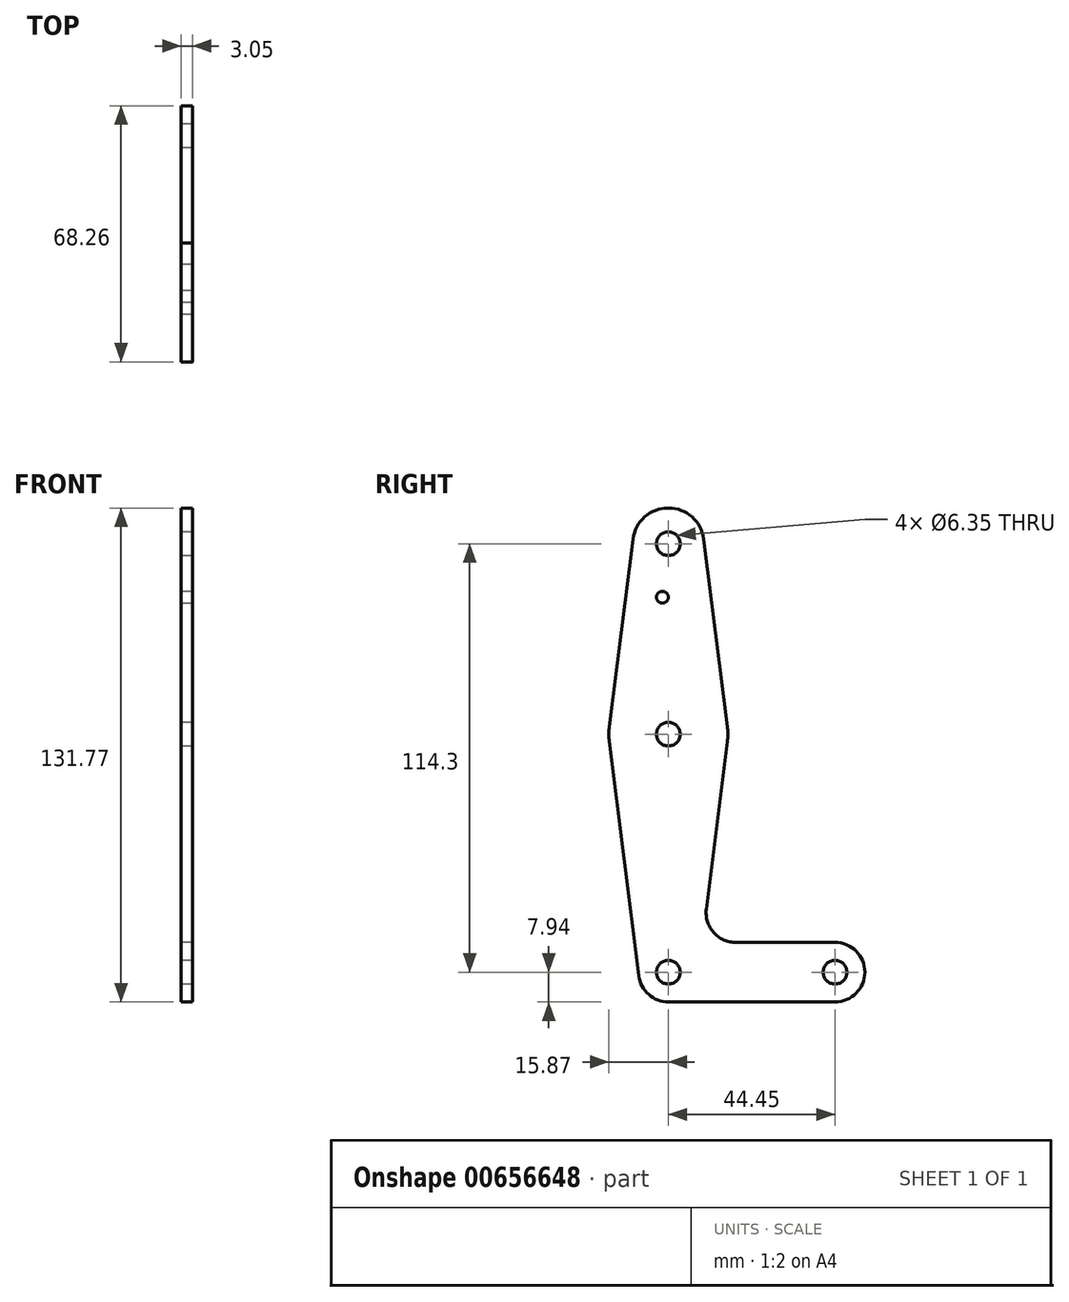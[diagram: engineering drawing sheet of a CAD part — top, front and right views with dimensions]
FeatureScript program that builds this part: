
annotation { "Feature Type Name" : "Feature", "Feature Type Description" : "" }
export const myFeature = defineFeature(function(context is Context, id is Id, definition is map)
    precondition{}
    {
        {
            var Q0;
            Q0=qCreatedBy(makeId("Right.planeOp"),FACE);
            var sketch = newSketch(context, id + "F0", { "sketchPlane" : qUnion([Q0])});
            skLineSegment(sketch, "E0", {"start": v(0, 114.3) * mm, "end": v(0, 0) * mm, "construction": true});
            skLineSegment(sketch, "E1", {"start": v(0, 0) * mm, "end": v(44.45, 0) * mm, "construction": true});
            skCircle(sketch, "E2", {"center": v(0, 114.3) * mm, "radius": 9.53 * mm});
            skCircle(sketch, "E3", {"center": v(0, 63.5) * mm, "radius": 15.88 * mm});
            skCircle(sketch, "E4", {"center": v(0, 0) * mm, "radius": 7.94 * mm});
            skCircle(sketch, "E5", {"center": v(44.45, 0) * mm, "radius": 7.94 * mm});
            skLineSegment(sketch, "E6", {"start": v(-9.45, 115.5) * mm, "end": v(-15.75, 65.48) * mm});
            skLineSegment(sketch, "E7", {"start": v(-15.75, 61.52) * mm, "end": v(-7.88, -1) * mm});
            skLineSegment(sketch, "E8", {"start": v(9.45, 115.5) * mm, "end": v(15.75, 65.48) * mm});
            skLineSegment(sketch, "E9", {"start": v(15.75, 61.52) * mm, "end": v(10.13, 16.88) * mm});
            skLineSegment(sketch, "E10", {"start": v(0, -7.94) * mm, "end": v(44.45, -7.94) * mm});
            skLineSegment(sketch, "E11", {"start": v(44.45, 7.94) * mm, "end": v(18.01, 7.94) * mm});
            skCircle(sketch, "E12", {"center": v(-1.59, 100.03) * mm, "radius": 1.59 * mm});
            skCircle(sketch, "E13", {"center": v(0, 114.3) * mm, "radius": 3.18 * mm});
            skCircle(sketch, "E14", {"center": v(0, 63.5) * mm, "radius": 3.18 * mm});
            skCircle(sketch, "E15", {"center": v(0, 0) * mm, "radius": 3.18 * mm});
            skCircle(sketch, "E16", {"center": v(44.45, 0) * mm, "radius": 3.18 * mm});
            skArc(sketch, "E17.filletArc", {"start": v(10.13, 16.88) * mm, "mid": v(12.05, 10.63) * mm, "end": v(18.01, 7.94) * mm});
            skSolve(sketch);
        }
        {
            var Q0;
            Q0 = qSketchRegion(id + "F0", true);
            extrude(context, id + "F1", {"entities" : qUnion([Q0]), "depth" : 3.05 * mm, "offsetDistance" : 25.4 * mm});
        }
    });
